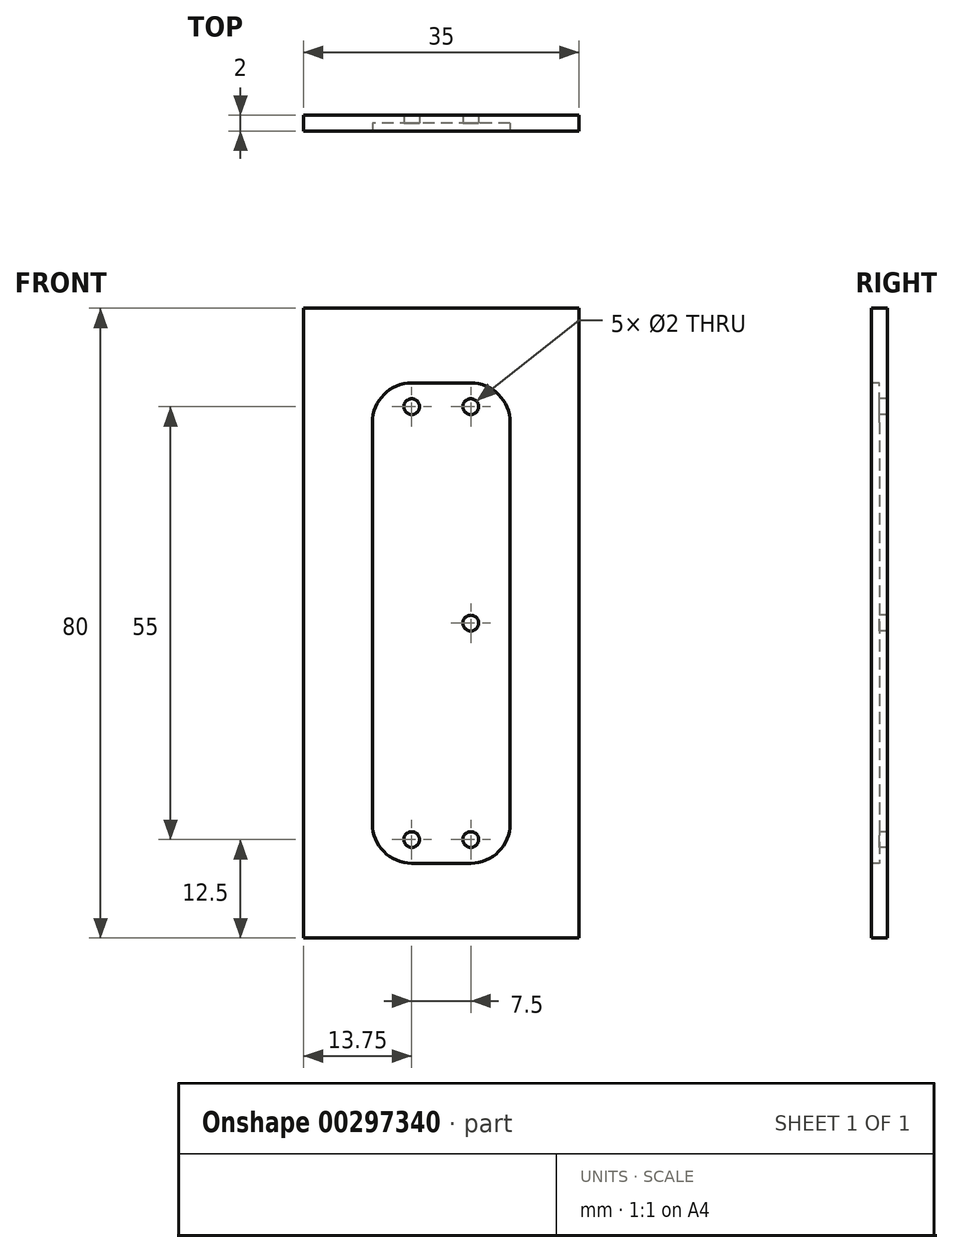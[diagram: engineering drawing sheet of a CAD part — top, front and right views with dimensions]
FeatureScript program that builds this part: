
annotation { "Feature Type Name" : "Feature", "Feature Type Description" : "" }
export const myFeature = defineFeature(function(context is Context, id is Id, definition is map)
    precondition{}
    {
        {
            var Q0;
            Q0=qCreatedBy(makeId("Front.planeOp"),FACE);
            var sketch = newSketch(context, id + "F0", { "sketchPlane" : qUnion([Q0])});
            skLineSegment(sketch, "E0.bottom", {"start": v(17.5, 40) * mm, "end": v(-17.5, 40) * mm});
            skLineSegment(sketch, "E0.top", {"start": v(17.5, -40) * mm, "end": v(-17.5, -40) * mm});
            skLineSegment(sketch, "E0.left", {"start": v(17.5, 40) * mm, "end": v(17.5, -40) * mm});
            skLineSegment(sketch, "E0.right", {"start": v(-17.5, 40) * mm, "end": v(-17.5, -40) * mm});
            skPoint(sketch, "E0.middle", {"position": v(0, 0) * mm});
            skSolve(sketch);
        }
        {
            var Q0;
            Q0 = qSketchRegion(id + "F0", true);
            extrude(context, id + "F1", {"entities" : qUnion([Q0]), "depth" : 2 * mm});
        }
        {
            var Q0;
            Q0=makeQuery(id+"F1.opExtrude","CAP_FACE",FACE,{"disambiguationData":[OSD([sQuery(id+"F0.wireOp",EDGE,"E0.bottom"),sQuery(id+"F0.wireOp",EDGE,"E0.top"),sQuery(id+"F0.wireOp",EDGE,"E0.left"),sQuery(id+"F0.wireOp",EDGE,"E0.right")])],"isStart":false});
            var sketch = newSketch(context, id + "F2", { "sketchPlane" : qUnion([Q0])});
            skLineSegment(sketch, "E1.bottom", {"start": v(8.75, 30.5) * mm, "end": v(-8.75, 30.5) * mm});
            skLineSegment(sketch, "E1.top", {"start": v(8.75, -30.5) * mm, "end": v(-8.75, -30.5) * mm});
            skLineSegment(sketch, "E1.left", {"start": v(8.75, 30.5) * mm, "end": v(8.75, -30.5) * mm});
            skLineSegment(sketch, "E1.right", {"start": v(-8.75, 30.5) * mm, "end": v(-8.75, -30.5) * mm});
            skPoint(sketch, "E1.middle", {"position": v(0, 0) * mm});
            skSolve(sketch);
        }
        {
            var Q0;
            Q0 = qSketchRegion(id + "F2", true);
            extrude(context, id + "F3", {"entities" : qUnion([Q0]), "operationType" : NewBodyOperationType.REMOVE, "oppositeDirection" : true, "depth" : 1 * mm});
        }
        {
            var Q0;
            Q0=makeQuery(id+"F3.boolean.opBoolean","COPY",FACE,{"derivedFrom":makeQuery(id+"F3.opExtrude","CAP_FACE",FACE,{"disambiguationData":[OSD([sQuery(id+"F2.wireOp",EDGE,"E1.bottom"),sQuery(id+"F2.wireOp",EDGE,"E1.top"),sQuery(id+"F2.wireOp",EDGE,"E1.left"),sQuery(id+"F2.wireOp",EDGE,"E1.right")])],"isStart":false})});
            var sketch = newSketch(context, id + "F4", { "sketchPlane" : qUnion([Q0])});
            skLineSegment(sketch, "E2.bottom", {"start": v(3.75, 27.5) * mm, "end": v(-3.75, 27.5) * mm, "construction": true});
            skLineSegment(sketch, "E2.top", {"start": v(3.75, -27.5) * mm, "end": v(-3.75, -27.5) * mm, "construction": true});
            skLineSegment(sketch, "E2.left", {"start": v(3.75, 27.5) * mm, "end": v(3.75, -27.5) * mm, "construction": true});
            skLineSegment(sketch, "E2.right", {"start": v(-3.75, 27.5) * mm, "end": v(-3.75, -27.5) * mm, "construction": true});
            skPoint(sketch, "E2.middle", {"position": v(0, 0) * mm});
            skCircle(sketch, "E3", {"center": v(3.75, 27.5) * mm, "radius": 1 * mm});
            skCircle(sketch, "E4", {"center": v(3.75, 0) * mm, "radius": 1 * mm});
            skCircle(sketch, "E5", {"center": v(3.75, -27.5) * mm, "radius": 1 * mm});
            skCircle(sketch, "E6", {"center": v(-3.75, 27.5) * mm, "radius": 1 * mm});
            skCircle(sketch, "E7", {"center": v(-3.75, -27.5) * mm, "radius": 1 * mm});
            skSolve(sketch);
        }
        {
            var Q0;
            Q0 = qSketchRegion(id + "F4", true);
            extrude(context, id + "F5", {"entities" : qUnion([Q0]), "operationType" : NewBodyOperationType.REMOVE, "oppositeDirection" : true, "depth" : 25 * mm});
        }
        {
            var Q0;
            Q0=makeQuery(id+"F3.boolean.opBoolean","COPY",EDGE,{"derivedFrom":makeQuery(id+"F3.opExtrude","SWEPT_EDGE",EDGE,{"disambiguationData":[OSD([sQuery(id+"F2.wireOp",EDGE,"E1.top"),sQuery(id+"F2.wireOp",EDGE,"E1.right")])]})});
            var Q1;
            Q1=makeQuery(id+"F3.boolean.opBoolean","COPY",EDGE,{"derivedFrom":makeQuery(id+"F3.opExtrude","SWEPT_EDGE",EDGE,{"disambiguationData":[OSD([sQuery(id+"F2.wireOp",EDGE,"E1.top"),sQuery(id+"F2.wireOp",EDGE,"E1.left")])]})});
            var Q2;
            Q2=makeQuery(id+"F3.boolean.opBoolean","COPY",EDGE,{"derivedFrom":makeQuery(id+"F3.opExtrude","SWEPT_EDGE",EDGE,{"disambiguationData":[OSD([sQuery(id+"F2.wireOp",EDGE,"E1.bottom"),sQuery(id+"F2.wireOp",EDGE,"E1.right")])]})});
            var Q3;
            Q3=makeQuery(id+"F3.boolean.opBoolean","COPY",EDGE,{"derivedFrom":makeQuery(id+"F3.opExtrude","SWEPT_EDGE",EDGE,{"disambiguationData":[OSD([sQuery(id+"F2.wireOp",EDGE,"E1.bottom"),sQuery(id+"F2.wireOp",EDGE,"E1.left")])]})});
            fillet(context, id + "F6", {"entities" : qUnion([Q0, Q1, Q2, Q3]), "radius" : 5 * mm, "tangentPropagation" : true, "allowEdgeOverflow" : false});
        }
    });
